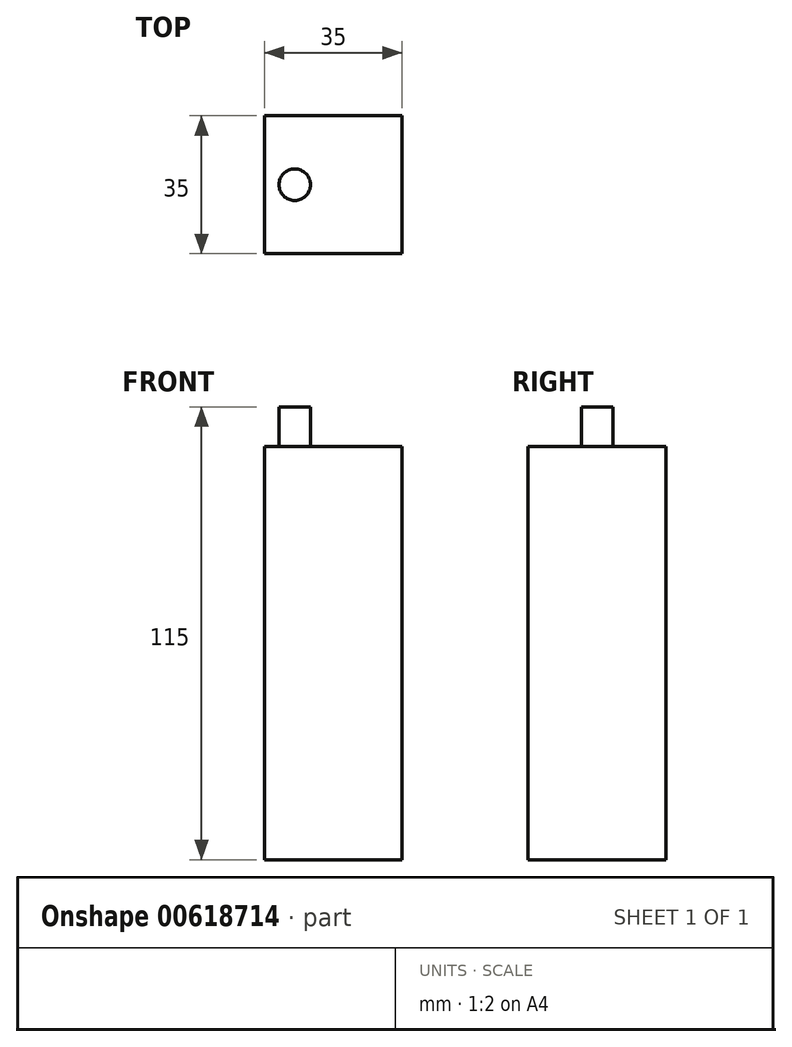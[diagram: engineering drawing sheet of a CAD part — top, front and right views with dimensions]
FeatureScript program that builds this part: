
annotation { "Feature Type Name" : "Feature", "Feature Type Description" : "" }
export const myFeature = defineFeature(function(context is Context, id is Id, definition is map)
    precondition{}
    {
        {
            var Q0;
            Q0=qCreatedBy(makeId("Front.planeOp"),FACE);
            var sketch = newSketch(context, id + "F0", { "sketchPlane" : qUnion([Q0])});
            skLineSegment(sketch, "E0.bottom", {"start": v(-25.62, 0) * mm, "end": v(9.38, 0) * mm});
            skLineSegment(sketch, "E0.top", {"start": v(-25.62, 105) * mm, "end": v(9.38, 105) * mm});
            skLineSegment(sketch, "E0.left", {"start": v(-25.62, 0) * mm, "end": v(-25.62, 105) * mm});
            skLineSegment(sketch, "E0.right", {"start": v(9.38, 0) * mm, "end": v(9.38, 105) * mm});
            skSolve(sketch);
        }
        {
            var Q0;
            Q0=qSketchRegion(id+"F0",true);
            extrude(context, id + "F1", {"entities" : qUnion([Q0]), "endBound" : BoundingType.SYMMETRIC, "depth" : 35 * mm, "hasSecondDirection" : true, "secondDirectionOppositeDirection" : true, "secondDirectionDepth" : 20 * mm, "offsetDistance" : 25 * mm});
        }
        {
            var Q0;
            Q0=makeQuery(id+"F1.opExtrude","SWEPT_FACE",FACE,{"disambiguationData":[OSD([sQuery(id+"F0.wireOp",EDGE,"E0.top")])]});
            var sketch = newSketch(context, id + "F2", { "sketchPlane" : qUnion([Q0])});
            skCircle(sketch, "E1", {"center": v(-17.92, 0) * mm, "radius": 4 * mm});
            skPoint(sketch, "E1.centerSnap0", {"position": v(-25.62, 0) * mm});
            skSolve(sketch);
        }
        {
            var Q0;
            Q0=makeQuery(id+"F2.imprint","IMPRINT",FACE,{"disambiguationData":[TD([[makeQuery(id+"F2.imprint","IMPRINT",EDGE,{"derivedFrom":sQuery(id+"F2.wireOp",EDGE,"E1")}),1.0]])]});
            extrude(context, id + "F3", {"entities" : qUnion([Q0]), "operationType" : NewBodyOperationType.ADD, "depth" : 10 * mm});
        }
    });
